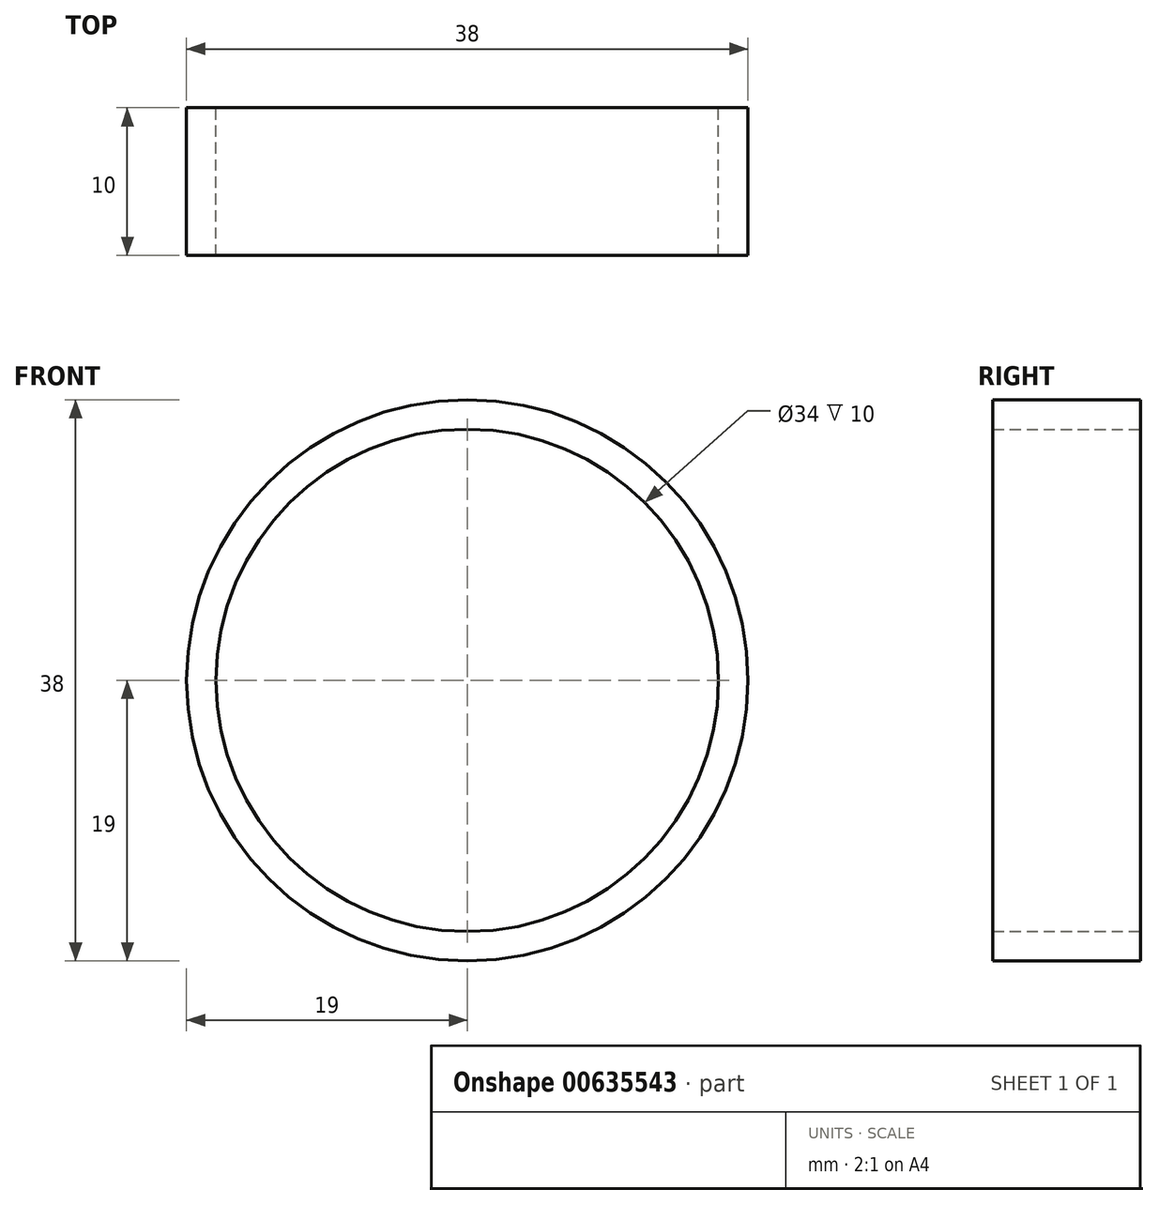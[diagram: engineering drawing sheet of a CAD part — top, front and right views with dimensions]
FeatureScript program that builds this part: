
annotation { "Feature Type Name" : "Feature", "Feature Type Description" : "" }
export const myFeature = defineFeature(function(context is Context, id is Id, definition is map)
    precondition{}
    {
        {
            var Q0;
            Q0=qCreatedBy(makeId("Front.planeOp"),FACE);
            var sketch = newSketch(context, id + "F0", { "sketchPlane" : qUnion([Q0])});
            skPoint(sketch, "E0", {"position": v(0, 0) * mm});
            skPoint(sketch, "E1", {"position": v(-33.47, -12.26) * mm});
            skCircle(sketch, "E2", {"center": v(0, 0) * mm, "radius": 1 * mm});
            skCircle(sketch, "E3.0.1.0", {"center": v(0, 10) * mm, "radius": 1 * mm});
            skCircle(sketch, "E3.0.2.0", {"center": v(0, 20) * mm, "radius": 1 * mm});
            skCircle(sketch, "E3.0.3.0", {"center": v(0, 30) * mm, "radius": 1 * mm});
            skCircle(sketch, "E3.0.4.0", {"center": v(0, 40) * mm, "radius": 1 * mm});
            skCircle(sketch, "E3.0.5.0", {"center": v(0, 50) * mm, "radius": 1 * mm});
            skCircle(sketch, "E3.1.0.0", {"center": v(10, 0) * mm, "radius": 1 * mm});
            skCircle(sketch, "E3.1.1.0", {"center": v(10, 10) * mm, "radius": 1 * mm});
            skCircle(sketch, "E3.1.2.0", {"center": v(10, 20) * mm, "radius": 1 * mm});
            skCircle(sketch, "E3.1.3.0", {"center": v(10, 30) * mm, "radius": 1 * mm});
            skCircle(sketch, "E3.1.4.0", {"center": v(10, 40) * mm, "radius": 1 * mm});
            skCircle(sketch, "E3.1.5.0", {"center": v(10, 50) * mm, "radius": 1 * mm});
            skCircle(sketch, "E3.2.0.0", {"center": v(20, 0) * mm, "radius": 1 * mm});
            skCircle(sketch, "E3.2.1.0", {"center": v(20, 10) * mm, "radius": 1 * mm});
            skCircle(sketch, "E3.2.2.0", {"center": v(20, 20) * mm, "radius": 1 * mm});
            skCircle(sketch, "E3.2.3.0", {"center": v(20, 30) * mm, "radius": 1 * mm});
            skCircle(sketch, "E3.2.4.0", {"center": v(20, 40) * mm, "radius": 1 * mm});
            skCircle(sketch, "E3.2.5.0", {"center": v(20, 50) * mm, "radius": 1 * mm});
            skCircle(sketch, "E3.3.0.0", {"center": v(30, 0) * mm, "radius": 1 * mm});
            skCircle(sketch, "E3.3.1.0", {"center": v(30, 10) * mm, "radius": 1 * mm});
            skCircle(sketch, "E3.3.2.0", {"center": v(30, 20) * mm, "radius": 1 * mm});
            skCircle(sketch, "E3.3.3.0", {"center": v(30, 30) * mm, "radius": 1 * mm});
            skCircle(sketch, "E3.3.4.0", {"center": v(30, 40) * mm, "radius": 1 * mm});
            skCircle(sketch, "E3.3.5.0", {"center": v(30, 50) * mm, "radius": 1 * mm});
            skCircle(sketch, "E3.4.0.0", {"center": v(40, 0) * mm, "radius": 1 * mm});
            skCircle(sketch, "E3.4.1.0", {"center": v(40, 10) * mm, "radius": 1 * mm});
            skCircle(sketch, "E3.4.2.0", {"center": v(40, 20) * mm, "radius": 1 * mm});
            skCircle(sketch, "E3.4.3.0", {"center": v(40, 30) * mm, "radius": 1 * mm});
            skCircle(sketch, "E3.4.4.0", {"center": v(40, 40) * mm, "radius": 1 * mm});
            skCircle(sketch, "E3.4.5.0", {"center": v(40, 50) * mm, "radius": 1 * mm});
            skCircle(sketch, "E3.5.0.0", {"center": v(50, 0) * mm, "radius": 1 * mm});
            skCircle(sketch, "E3.5.1.0", {"center": v(50, 10) * mm, "radius": 1 * mm});
            skCircle(sketch, "E3.5.2.0", {"center": v(50, 20) * mm, "radius": 1 * mm});
            skCircle(sketch, "E3.5.3.0", {"center": v(50, 30) * mm, "radius": 1 * mm});
            skCircle(sketch, "E3.5.4.0", {"center": v(50, 40) * mm, "radius": 1 * mm});
            skCircle(sketch, "E3.5.5.0", {"center": v(50, 50) * mm, "radius": 1 * mm});
            skLineSegment(sketch, "E3.direction1", {"start": v(0, 0) * mm, "end": v(10, 0) * mm, "construction": true});
            skLineSegment(sketch, "E3.direction2", {"start": v(0, 0) * mm, "end": v(0, 10) * mm, "construction": true});
            skSolve(sketch);
        }
        {
            var Q0;
            Q0=qCreatedBy(makeId("Front.planeOp"),FACE);
            cPlane(context, id + "F1", {"entities" : qUnion([Q0]), "cplaneType" : CPlaneType.OFFSET, "offset" : 50 * mm, "width" : 150 * mm, "height" : 150 * mm});
        }
        {
            var Q0;
            Q0=qCreatedBy(id+"F1.planeOp",FACE);
            var sketch = newSketch(context, id + "F2", { "sketchPlane" : qUnion([Q0])});
            skPoint(sketch, "E4", {"position": v(30, 30) * mm});
            skCircle(sketch, "E5", {"center": v(30, 30) * mm, "radius": 17 * mm});
            skCircle(sketch, "E6", {"center": v(30, 30) * mm, "radius": 19 * mm});
            skSolve(sketch);
        }
        {
            var Q0;
            Q0 = qSketchRegion(id + "F2", true);
            extrude(context, id + "F3", {"entities" : qUnion([Q0]), "depth" : 5 * mm, "offsetDistance" : 25 * mm, "hasSecondDirection" : true, "secondDirectionOppositeDirection" : true, "secondDirectionDepth" : 5 * mm});
        }
    });
